# Revit family: CENTUM Gewindestift links rechts
name_source: partatom
category: HLS-Bauteile
revit_build: Autodesk Revit 2017 (Build: 20190507_1515(x64)
units: mm (PartAtom-declared; Revit-internal decimal feet)

## family parameters
Arbeitsebenenbasiert = Nein
Beim Laden mit Abzugskörper schneiden = Nein
Bemaßung runder Anschluss = Durchmesser verwenden
Gemeinsam genutzt = Ja
Immer vertikal = Nein
Raumberechnungspunkt = Nein
Teiletyp = Normal

## types (2) — shared parameters
Fabrikat = MEFA
Festigkeitsklasse = 4.6
Firma = MEFA Befestigungs- und Montagesysteme GmbH
Kurztext1 = Gewindestift links-rechts
L = 250 mm  [stored 0.82021 ft]
Länge = 250 mm  [stored 0.82021 ft]
Länge Gewinde 1 = 130 mm
Länge Gewinde 2 = 80 mm
Material = Stahl
Mengeneinheit = St
Oberflaeche = feuerverzinkt
vpe = 1 St

## per-type parameters (varying)
| type | Artikelnummer | D | EAN | Gewicht | Gewicht pro Bauteil | Gewinde | Kurztext2 | L2 | L3 |
| Gewindestift L/R M16 | 1660007216 | 13 mm | 4250928449603 | 0.40 kg | 0.40 kg | M16 | M16 x 250 mm fvz FK 4.6 | 7 mm  [stored 0.0229659 ft] | 7 mm  [stored 0.0229659 ft] |
| Gewindestift L/R M12 | 1660007212 | 9 mm  [stored 0.0295276 ft] | 4250928449597 | 0.22 kg | 0.22 kg | M12 | M12 x 250 mm fvz FK 4.6 | 5 mm  [stored 0.0164042 ft] | 5 mm  [stored 0.0164042 ft] |

note: [stored X ft] marks values corroborated as IEEE doubles in the binary element streams (Revit-internal decimal feet)
